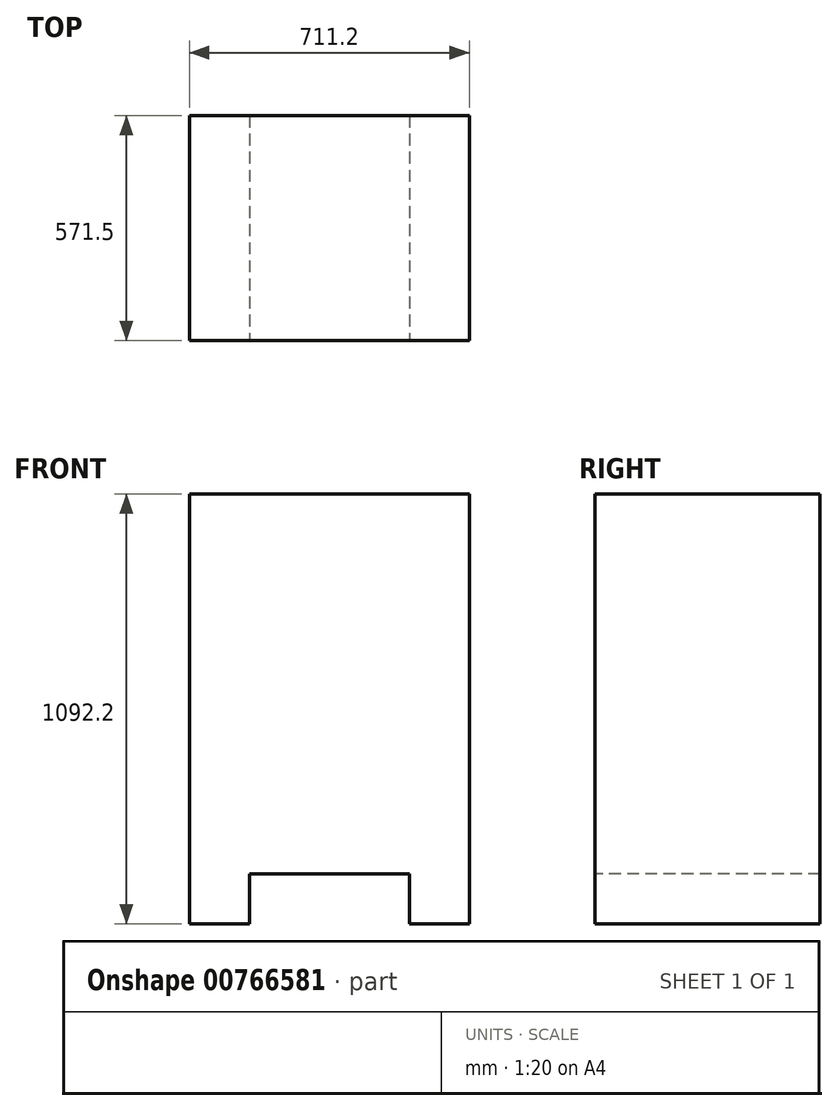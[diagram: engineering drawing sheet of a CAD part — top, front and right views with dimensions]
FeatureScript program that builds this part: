
annotation { "Feature Type Name" : "Feature", "Feature Type Description" : "" }
export const myFeature = defineFeature(function(context is Context, id is Id, definition is map)
    precondition{}
    {
        {
            var Q0;
            Q0=qCreatedBy(makeId("Top.planeOp"),FACE);
            var sketch = newSketch(context, id + "F0", { "sketchPlane" : qUnion([Q0])});
            skLineSegment(sketch, "E0.bottom", {"start": v(-355.6, 285.75) * mm, "end": v(355.6, 285.75) * mm});
            skLineSegment(sketch, "E0.top", {"start": v(-355.6, -285.75) * mm, "end": v(355.6, -285.75) * mm});
            skLineSegment(sketch, "E0.left", {"start": v(-355.6, 285.75) * mm, "end": v(-355.6, -285.75) * mm});
            skLineSegment(sketch, "E0.right", {"start": v(355.6, 285.75) * mm, "end": v(355.6, -285.75) * mm});
            skLineSegment(sketch, "E1", {"start": v(-355.6, 285.75) * mm, "end": v(355.6, -285.75) * mm, "construction": true});
            skSolve(sketch);
        }
        {
            var Q0;
            Q0=qSketchRegion(id+"F0",true);
            extrude(context, id + "F1", {"entities" : qUnion([Q0]), "depth" : 1092.2 * mm, "offsetDistance" : 25.4 * mm});
        }
        {
            var Q0;
            Q0=makeQuery(id+"F1.opExtrude","SWEPT_FACE",FACE,{"disambiguationData":[OSD([sQuery(id+"F0.wireOp",EDGE,"E0.top")])]});
            var sketch = newSketch(context, id + "F2", { "sketchPlane" : qUnion([Q0])});
            skLineSegment(sketch, "E2.bottom", {"start": v(-203.2, 0) * mm, "end": v(203.2, 0) * mm});
            skLineSegment(sketch, "E2.top", {"start": v(-203.2, 127) * mm, "end": v(203.2, 127) * mm});
            skLineSegment(sketch, "E2.left", {"start": v(-203.2, 0) * mm, "end": v(-203.2, 127) * mm});
            skLineSegment(sketch, "E2.right", {"start": v(203.2, 0) * mm, "end": v(203.2, 127) * mm});
            skSolve(sketch);
        }
        {
            var Q0;
            Q0=qSketchRegion(id+"F2",true);
            extrude(context, id + "F3", {"entities" : qUnion([Q0]), "operationType" : NewBodyOperationType.REMOVE, "endBound" : BoundingType.THROUGH_ALL, "oppositeDirection" : true, "depth" : 25.4 * mm, "offsetDistance" : 25.4 * mm});
        }
    });
